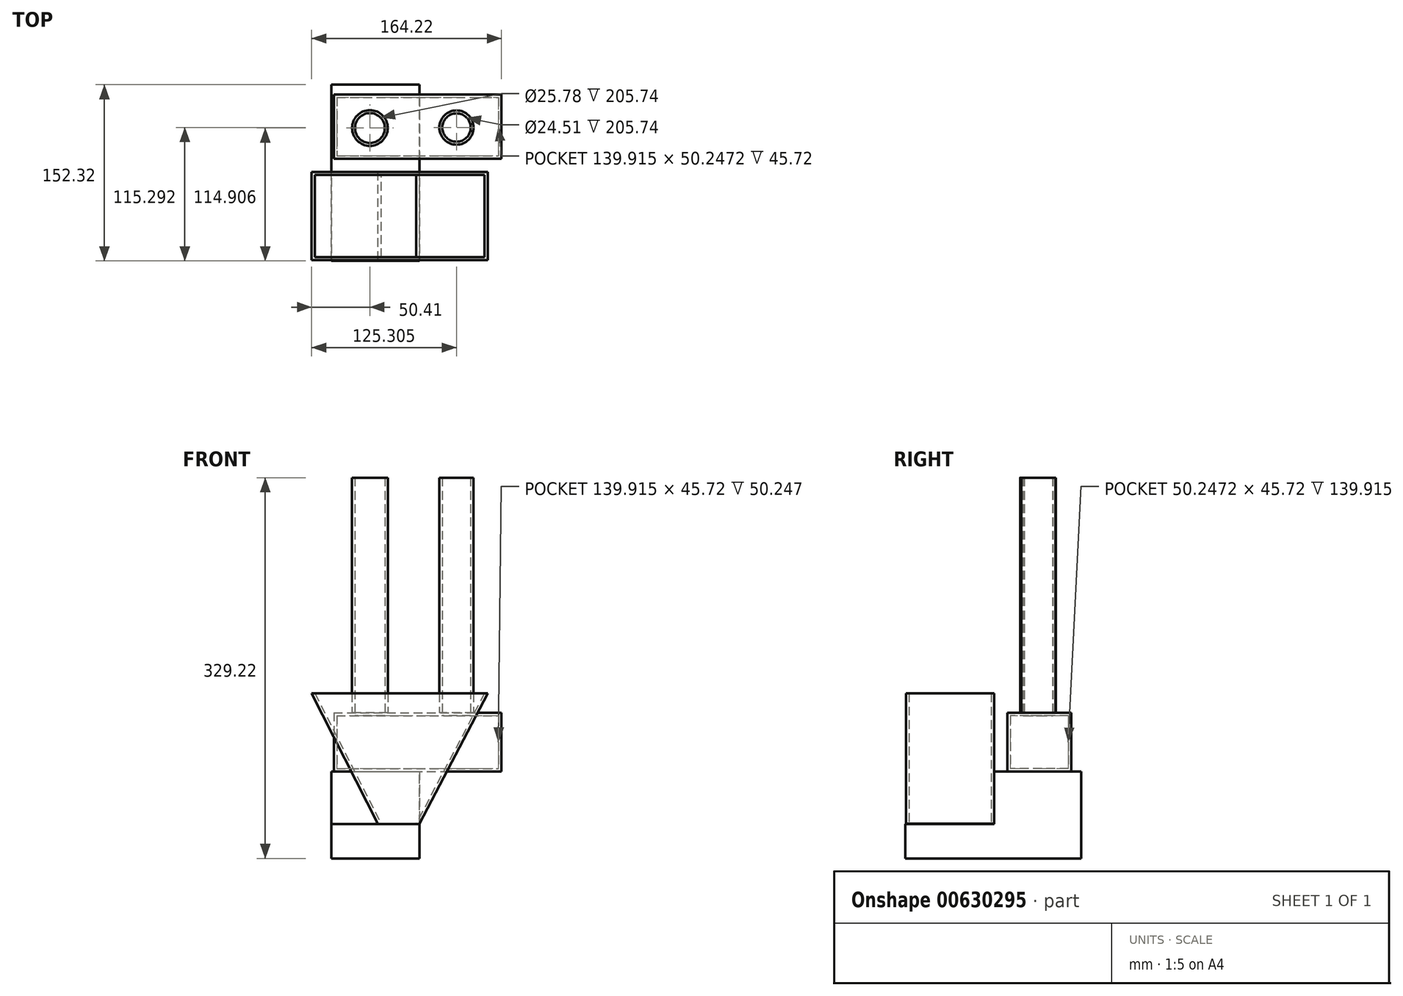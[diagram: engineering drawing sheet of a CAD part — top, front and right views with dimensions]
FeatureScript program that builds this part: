
annotation { "Feature Type Name" : "Feature", "Feature Type Description" : "" }
export const myFeature = defineFeature(function(context is Context, id is Id, definition is map)
    precondition{}
    {
        {
            var Q0;
            Q0=qCreatedBy(makeId("Front.planeOp"),FACE);
            var sketch = newSketch(context, id + "F0", { "sketchPlane" : qUnion([Q0])});
            skLineSegment(sketch, "E0", {"start": v(-93.43, 67.38) * mm, "end": v(58.97, 67.38) * mm});
            skLineSegment(sketch, "E1", {"start": v(-93.43, 67.38) * mm, "end": v(-35.86, -45.83) * mm});
            skLineSegment(sketch, "E2", {"start": v(58.97, 67.38) * mm, "end": v(-0.08, -45.06) * mm});
            skLineSegment(sketch, "E3", {"start": v(-35.86, -45.83) * mm, "end": v(-0.08, -45.06) * mm});
            skSolve(sketch);
        }
        {
            var Q0;
            Q0=makeQuery(id+"F0.imprint","IMPRINT",FACE,{"disambiguationData":[TD([[makeQuery(id+"F0.imprint","IMPRINT",EDGE,{"derivedFrom":sQuery(id+"F0.wireOp",EDGE,"E0")}),-1.0]])]});
            extrude(context, id + "F1", {"entities" : qUnion([Q0]), "depth" : 76.2 * mm, "offsetDistance" : 25.4 * mm});
        }
        {
            var Q0;
            Q0=makeQuery(id+"F1.opExtrude","SWEPT_FACE",FACE,{"disambiguationData":[OSD([sQuery(id+"F0.wireOp",EDGE,"E0")])]});
            var Q1;
            Q1=makeQuery(id+"F1.opExtrude","SWEPT_FACE",FACE,{"disambiguationData":[OSD([sQuery(id+"F0.wireOp",EDGE,"E3")])]});
            shell(context, id + "F2", {"entities" : qUnion([Q0, Q1]), "thickness" : 2.54 * mm});
        }
        {
            var Q0;
            Q0=qCreatedBy(makeId("Top.planeOp"),FACE);
            var sketch = newSketch(context, id + "F3", { "sketchPlane" : qUnion([Q0])});
            skLineSegment(sketch, "E4.bottom", {"start": v(-74.2, 66.85) * mm, "end": v(70.79, 66.85) * mm});
            skLineSegment(sketch, "E4.top", {"start": v(-74.2, 11.52) * mm, "end": v(70.79, 11.52) * mm});
            skLineSegment(sketch, "E4.left", {"start": v(-74.2, 66.85) * mm, "end": v(-74.2, 11.52) * mm});
            skLineSegment(sketch, "E4.right", {"start": v(70.79, 66.85) * mm, "end": v(70.79, 11.52) * mm});
            skCircle(sketch, "E5", {"center": v(-41.78, 38.7) * mm, "radius": 12.7 * mm});
            skCircle(sketch, "E6", {"center": v(32.15, 37.28) * mm, "radius": 12.7 * mm});
            skSolve(sketch);
        }
        {
            var Q0;
            Q0=makeQuery(id+"F3.imprint","IMPRINT",FACE,{"disambiguationData":[TD([[makeQuery(id+"F3.imprint","IMPRINT",EDGE,{"derivedFrom":sQuery(id+"F3.wireOp",EDGE,"E4.bottom")}),-1.0]])]});
            extrude(context, id + "F4", {"entities" : qUnion([Q0]), "depth" : 50.8 * mm, "offsetDistance" : 25.4 * mm});
        }
        {
            var Q0;
            Q0=qCreatedBy(makeId("Top.planeOp"),FACE);
            var sketch = newSketch(context, id + "F5", { "sketchPlane" : qUnion([Q0])});
            skCircle(sketch, "E7", {"center": v(-43.02, 38.03) * mm, "radius": 15.43 * mm});
            skCircle(sketch, "E8", {"center": v(31.87, 38.41) * mm, "radius": 14.8 * mm});
            skSolve(sketch);
        }
        {
            var Q0;
            Q0=makeQuery(id+"F5.imprint","IMPRINT",FACE,{"disambiguationData":[TD([[makeQuery(id+"F5.imprint","IMPRINT",EDGE,{"derivedFrom":sQuery(id+"F5.wireOp",EDGE,"E8")}),1.0]])]});
            var Q1;
            Q1=makeQuery(id+"F5.imprint","IMPRINT",FACE,{"disambiguationData":[TD([[makeQuery(id+"F5.imprint","IMPRINT",EDGE,{"derivedFrom":sQuery(id+"F5.wireOp",EDGE,"E7")}),1.0]])]});
            extrude(context, id + "F6", {"entities" : qUnion([Q0, Q1]), "operationType" : NewBodyOperationType.ADD, "depth" : 254 * mm, "offsetDistance" : 25.4 * mm});
        }
        {
            var Q0;
            Q0=qCreatedBy(makeId("Right.planeOp"),FACE);
            var sketch = newSketch(context, id + "F7", { "sketchPlane" : qUnion([Q0])});
            skLineSegment(sketch, "E9", {"start": v(0, 0) * mm, "end": v(75.44, 0) * mm});
            skLineSegment(sketch, "E10", {"start": v(75.44, 0) * mm, "end": v(75.44, -75.22) * mm});
            skLineSegment(sketch, "E11", {"start": v(75.44, -75.22) * mm, "end": v(-76.88, -75.22) * mm});
            skLineSegment(sketch, "E12", {"start": v(-76.88, -75.22) * mm, "end": v(-76.88, -45.66) * mm});
            skLineSegment(sketch, "E13", {"start": v(-76.88, -45.66) * mm, "end": v(0, -45.66) * mm});
            skLineSegment(sketch, "E14", {"start": v(0, -45.66) * mm, "end": v(0, 0) * mm});
            skSolve(sketch);
        }
        {
            var Q0;
            Q0=makeQuery(id+"F7.imprint","IMPRINT",FACE,{"disambiguationData":[TD([[makeQuery(id+"F7.imprint","IMPRINT",EDGE,{"derivedFrom":sQuery(id+"F7.wireOp",EDGE,"E9")}),-1.0]])]});
            extrude(context, id + "F8", {"entities" : qUnion([Q0]), "depth" : -76.2 * mm, "offsetDistance" : 25.4 * mm});
        }
        {
            var Q0;
            Q0=makeQuery(id+"F6.opExtrude","CAP_FACE",FACE,{"disambiguationData":[OSD([sQuery(id+"F5.wireOp",EDGE,"E8")])],"isStart":false});
            var Q1;
            Q1=makeQuery(id+"F6.opExtrude","CAP_FACE",FACE,{"disambiguationData":[OSD([sQuery(id+"F5.wireOp",EDGE,"E7")])],"isStart":false});
            shell(context, id + "F9", {"entities" : qUnion([Q0, Q1]), "thickness" : 2.54 * mm});
        }
    });
